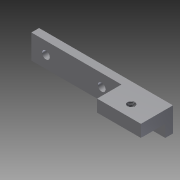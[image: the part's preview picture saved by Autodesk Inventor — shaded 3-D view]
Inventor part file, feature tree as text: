
AUTODESK INVENTOR PART (.ipt)
format: ipt  version: 2011 (Build 150239000, 239)  size: 110,592 bytes
history: native  units: in
note: dims shown in document units (in); Inventor stores cm internally (conversion verified against a paired STEP export)
features: sketch x5, extrude x3, hole x2, thread x1
ambient origin geometry x8: Origin, YZ Plane, XZ Plane, XY Plane, X Axis, Y Axis, Z Axis, Center Point
bodies: Solid1 (feature_tree)
feature tree (11):
  extrude  "Extrusion1"  Depth=0.3937in
  hole  "Hole1"  [1 undecoded]
  extrude  "Extrusion4"  Depth=0.7087in
  hole  "Hole3"  [1 undecoded]
  thread  "Thread2"  [1 undecoded]
  extrude  "Extrusion5"  Depth=0.0157in
  sketch  "Sketch1"  dims[d0=2.1654in d1=0.3937in]
  sketch  "Sketch3"  dims[d2=0.125in d3=0.0in d8=0.2362in]
  sketch  "Sketch6"  dims[d9=0.9016in]
  sketch  "Sketch7"  dims[d10=0.126in d11=0.75in d12=0.375in d13=0.25in d14=0.5635in d15=1.0in d16=0.8108in d32=0.7087in]
  sketch  "Sketch8"  dims[d33=0.1969in d34=0.3937in d35=0.0in d36=0.1181in d37=0.75in d38=0.375in d39=0.25in d40=0.5635in d41=1.0in d42=0.8108in d43=1.0in d44=0.0in d45=0.0157in d46=0.0079in d47=45.0deg d48=135.0deg d49=0.3937in d50=0.0in]
note: 3 required parameter values undecoded (feature->parameter linkage not recoverable at this tier; creation-order binding heuristic only, values carry confidence <= 0.55)
